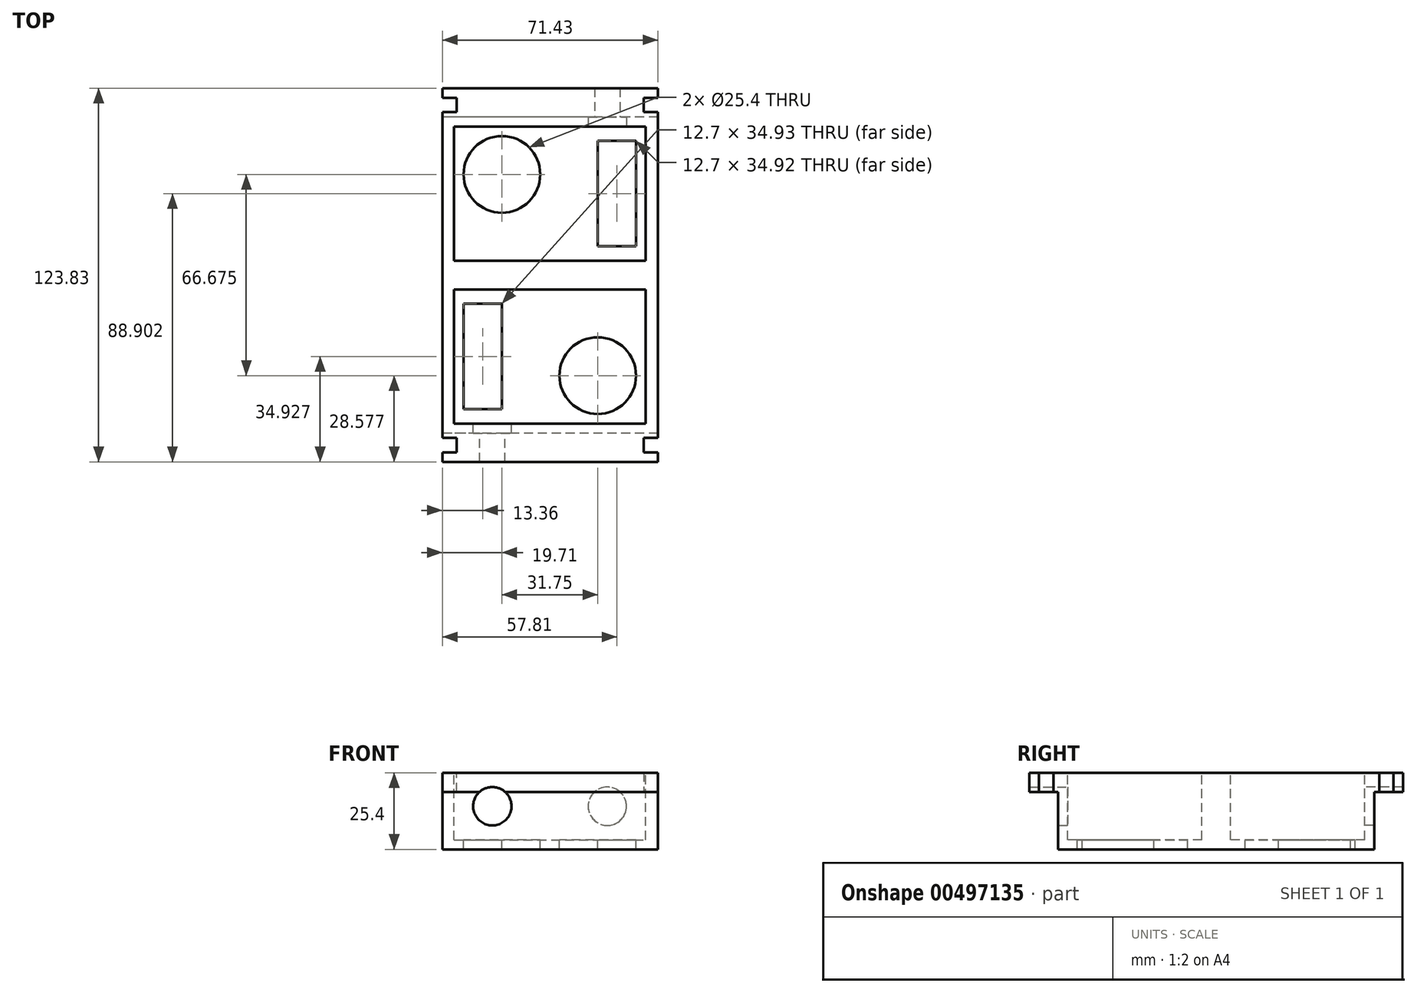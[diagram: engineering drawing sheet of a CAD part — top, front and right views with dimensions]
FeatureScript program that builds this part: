
annotation { "Feature Type Name" : "Feature", "Feature Type Description" : "" }
export const myFeature = defineFeature(function(context is Context, id is Id, definition is map)
    precondition{}
    {
        {
            var Q0;
            Q0=qCreatedBy(makeId("Top.planeOp"),FACE);
            var sketch = newSketch(context, id + "F0", { "sketchPlane" : qUnion([Q0])});
            skLineSegment(sketch, "E0.bottom", {"start": v(-33.34, 67.9) * mm, "end": v(38.09, 67.9) * mm});
            skLineSegment(sketch, "E0.top", {"start": v(-33.34, -55.92) * mm, "end": v(38.09, -55.92) * mm});
            skLineSegment(sketch, "E0.left", {"start": v(-33.34, 67.9) * mm, "end": v(-33.34, -55.92) * mm});
            skLineSegment(sketch, "E0.right", {"start": v(38.09, 67.9) * mm, "end": v(38.09, -55.92) * mm});
            skSolve(sketch);
        }
        {
            var Q0;
            Q0=makeQuery(id+"F0.imprint","IMPRINT",FACE,{"disambiguationData":[TD([[makeQuery(id+"F0.imprint","IMPRINT",EDGE,{"derivedFrom":sQuery(id+"F0.wireOp",EDGE,"E0.bottom")}),-1.0]])]});
            extrude(context, id + "F1", {"entities" : qUnion([Q0]), "depth" : 25.4 * mm});
        }
        {
            var Q0;
            Q0=makeQuery(id+"F1.opExtrude","CAP_FACE",FACE,{"disambiguationData":[OSD([sQuery(id+"F0.wireOp",EDGE,"E0.bottom"),sQuery(id+"F0.wireOp",EDGE,"E0.top"),sQuery(id+"F0.wireOp",EDGE,"E0.left"),sQuery(id+"F0.wireOp",EDGE,"E0.right")])],"isStart":false});
            var sketch = newSketch(context, id + "F2", { "sketchPlane" : qUnion([Q0])});
            skLineSegment(sketch, "E1.bottom", {"start": v(-29.5, 55.2) * mm, "end": v(34, 55.2) * mm});
            skLineSegment(sketch, "E1.top", {"start": v(-29.5, 10.76) * mm, "end": v(34, 10.76) * mm});
            skLineSegment(sketch, "E1.left", {"start": v(-29.5, 55.2) * mm, "end": v(-29.5, 10.76) * mm});
            skLineSegment(sketch, "E1.right", {"start": v(34, 55.2) * mm, "end": v(34, 10.76) * mm});
            skLineSegment(sketch, "E2.bottom", {"start": v(-29.5, 1.23) * mm, "end": v(34, 1.23) * mm});
            skLineSegment(sketch, "E2.top", {"start": v(-29.5, -43.22) * mm, "end": v(34, -43.22) * mm});
            skLineSegment(sketch, "E2.left", {"start": v(-29.5, 1.23) * mm, "end": v(-29.5, -43.22) * mm});
            skLineSegment(sketch, "E2.right", {"start": v(34, 1.23) * mm, "end": v(34, -43.22) * mm});
            skSolve(sketch);
        }
        {
            var Q0;
            Q0=makeQuery(id+"F2.imprint","IMPRINT",FACE,{"disambiguationData":[TD([[makeQuery(id+"F2.imprint","IMPRINT",EDGE,{"derivedFrom":sQuery(id+"F2.wireOp",EDGE,"E1.bottom")}),-1.0]])]});
            var Q1;
            Q1=makeQuery(id+"F2.imprint","IMPRINT",FACE,{"disambiguationData":[TD([[makeQuery(id+"F2.imprint","IMPRINT",EDGE,{"derivedFrom":sQuery(id+"F2.wireOp",EDGE,"E2.bottom")}),-1.0]])]});
            extrude(context, id + "F3", {"entities" : qUnion([Q0, Q1]), "operationType" : NewBodyOperationType.REMOVE, "oppositeDirection" : true, "depth" : 22.22 * mm});
        }
        {
            var Q0;
            Q0=makeQuery(id+"F1.opExtrude","SWEPT_FACE",FACE,{"disambiguationData":[OSD([sQuery(id+"F0.wireOp",EDGE,"E0.right")])]});
            var sketch = newSketch(context, id + "F4", { "sketchPlane" : qUnion([Q0])});
            skLineSegment(sketch, "E3.bottom", {"start": v(64.73, 25.4) * mm, "end": v(59.97, 25.4) * mm});
            skLineSegment(sketch, "E3.top", {"start": v(64.73, 0) * mm, "end": v(59.97, 0) * mm});
            skLineSegment(sketch, "E3.left", {"start": v(64.73, 25.4) * mm, "end": v(64.73, 0) * mm});
            skLineSegment(sketch, "E3.right", {"start": v(59.97, 25.4) * mm, "end": v(59.97, 0) * mm});
            skLineSegment(sketch, "E4.bottom", {"start": v(-47.98, 25.4) * mm, "end": v(-52.74, 25.4) * mm});
            skLineSegment(sketch, "E4.top", {"start": v(-47.98, 0) * mm, "end": v(-52.74, 0) * mm});
            skLineSegment(sketch, "E4.left", {"start": v(-47.98, 25.4) * mm, "end": v(-47.98, 0) * mm});
            skLineSegment(sketch, "E4.right", {"start": v(-52.74, 25.4) * mm, "end": v(-52.74, 0) * mm});
            skSolve(sketch);
        }
        {
            var Q0;
            Q0=makeQuery(id+"F4.imprint","IMPRINT",FACE,{"disambiguationData":[TD([[makeQuery(id+"F4.imprint","IMPRINT",EDGE,{"derivedFrom":sQuery(id+"F4.wireOp",EDGE,"E3.bottom")}),1.0]])]});
            var Q1;
            Q1=makeQuery(id+"F4.imprint","IMPRINT",FACE,{"disambiguationData":[TD([[makeQuery(id+"F4.imprint","IMPRINT",EDGE,{"derivedFrom":sQuery(id+"F4.wireOp",EDGE,"E4.bottom")}),1.0]])]});
            extrude(context, id + "F5", {"entities" : qUnion([Q0, Q1]), "operationType" : NewBodyOperationType.REMOVE, "oppositeDirection" : true, "depth" : 4.76 * mm});
        }
        {
            var Q0;
            Q0=makeQuery(id+"F1.opExtrude","SWEPT_FACE",FACE,{"disambiguationData":[OSD([sQuery(id+"F0.wireOp",EDGE,"E0.left")])]});
            var sketch = newSketch(context, id + "F6", { "sketchPlane" : qUnion([Q0])});
            skLineSegment(sketch, "E5.bottom", {"start": v(-64.73, 0) * mm, "end": v(-59.97, 0) * mm});
            skLineSegment(sketch, "E5.top", {"start": v(-64.73, 25.4) * mm, "end": v(-59.97, 25.4) * mm});
            skLineSegment(sketch, "E5.left", {"start": v(-64.73, 0) * mm, "end": v(-64.73, 25.4) * mm});
            skLineSegment(sketch, "E5.right", {"start": v(-59.97, 0) * mm, "end": v(-59.97, 25.4) * mm});
            skLineSegment(sketch, "E6.bottom", {"start": v(47.98, 0) * mm, "end": v(52.74, 0) * mm});
            skLineSegment(sketch, "E6.top", {"start": v(47.98, 25.4) * mm, "end": v(52.74, 25.4) * mm});
            skLineSegment(sketch, "E6.left", {"start": v(47.98, 0) * mm, "end": v(47.98, 25.4) * mm});
            skLineSegment(sketch, "E6.right", {"start": v(52.74, 0) * mm, "end": v(52.74, 25.4) * mm});
            skSolve(sketch);
        }
        {
            var Q0;
            Q0=makeQuery(id+"F6.imprint","IMPRINT",FACE,{"disambiguationData":[TD([[makeQuery(id+"F6.imprint","IMPRINT",EDGE,{"derivedFrom":sQuery(id+"F6.wireOp",EDGE,"E5.bottom")}),1.0]])]});
            var Q1;
            Q1=makeQuery(id+"F6.imprint","IMPRINT",FACE,{"disambiguationData":[TD([[makeQuery(id+"F6.imprint","IMPRINT",EDGE,{"derivedFrom":sQuery(id+"F6.wireOp",EDGE,"E6.bottom")}),1.0]])]});
            extrude(context, id + "F7", {"entities" : qUnion([Q0, Q1]), "operationType" : NewBodyOperationType.REMOVE, "oppositeDirection" : true, "depth" : 4.76 * mm});
        }
        {
            var Q0;
            Q0=makeQuery(id+"F1.opExtrude","CAP_FACE",FACE,{"disambiguationData":[OSD([sQuery(id+"F0.wireOp",EDGE,"E0.bottom"),sQuery(id+"F0.wireOp",EDGE,"E0.top"),sQuery(id+"F0.wireOp",EDGE,"E0.left"),sQuery(id+"F0.wireOp",EDGE,"E0.right")])],"isStart":true});
            var sketch = newSketch(context, id + "F8", { "sketchPlane" : qUnion([Q0])});
            skLineSegment(sketch, "E7.bottom", {"start": v(38.09, -67.9) * mm, "end": v(-33.34, -67.9) * mm});
            skLineSegment(sketch, "E7.top", {"start": v(38.09, -58.38) * mm, "end": v(-33.34, -58.38) * mm});
            skLineSegment(sketch, "E7.left", {"start": v(38.09, -67.9) * mm, "end": v(38.09, -58.38) * mm});
            skLineSegment(sketch, "E7.right", {"start": v(-33.34, -67.9) * mm, "end": v(-33.34, -58.38) * mm});
            skSolve(sketch);
        }
        {
            var Q0;
            {var subQ13=sQuery(id+"F8.wireOp",EDGE,"E7.bottom");Q0=makeQuery(id+"F8.imprint","IMPRINT",FACE,{"disambiguationData":[TD([[makeQuery(id+"F8.imprint","IMPRINT",EDGE,{"derivedFrom":subQ13}),1.0]])]});}
            extrude(context, id + "F9", {"entities" : qUnion([Q0]), "operationType" : NewBodyOperationType.REMOVE, "oppositeDirection" : true, "depth" : 19.05 * mm});
        }
        {
            var Q0;
            Q0=makeQuery(id+"F1.opExtrude","CAP_FACE",FACE,{"disambiguationData":[OSD([sQuery(id+"F0.wireOp",EDGE,"E0.bottom"),sQuery(id+"F0.wireOp",EDGE,"E0.top"),sQuery(id+"F0.wireOp",EDGE,"E0.left"),sQuery(id+"F0.wireOp",EDGE,"E0.right")])],"isStart":true});
            var sketch = newSketch(context, id + "F10", { "sketchPlane" : qUnion([Q0])});
            skLineSegment(sketch, "E8.bottom", {"start": v(38.09, 55.92) * mm, "end": v(-33.34, 55.92) * mm});
            skLineSegment(sketch, "E8.top", {"start": v(38.09, 46.4) * mm, "end": v(-33.34, 46.4) * mm});
            skLineSegment(sketch, "E8.left", {"start": v(38.09, 55.92) * mm, "end": v(38.09, 46.4) * mm});
            skLineSegment(sketch, "E8.right", {"start": v(-33.34, 55.92) * mm, "end": v(-33.34, 46.4) * mm});
            skSolve(sketch);
        }
        {
            var Q0;
            {var subQ6=sQuery(id+"F10.wireOp",EDGE,"E8.bottom");Q0=makeQuery(id+"F10.imprint","IMPRINT",FACE,{"disambiguationData":[TD([[makeQuery(id+"F10.imprint","IMPRINT",EDGE,{"derivedFrom":subQ6}),-1.0]])]});}
            extrude(context, id + "F11", {"entities" : qUnion([Q0]), "operationType" : NewBodyOperationType.REMOVE, "oppositeDirection" : true, "depth" : 19.05 * mm});
        }
        {
            var Q0;
            Q0=makeQuery(id+"F3.boolean.opBoolean","COPY",FACE,{"derivedFrom":makeQuery(id+"F3.opExtrude","CAP_FACE",FACE,{"disambiguationData":[OSD([sQuery(id+"F2.wireOp",EDGE,"E1.bottom"),sQuery(id+"F2.wireOp",EDGE,"E1.top"),sQuery(id+"F2.wireOp",EDGE,"E1.left"),sQuery(id+"F2.wireOp",EDGE,"E1.right")])],"isStart":false})});
            var sketch = newSketch(context, id + "F12", { "sketchPlane" : qUnion([Q0])});
            skCircle(sketch, "E9", {"center": v(-13.63, 39.33) * mm, "radius": 12.7 * mm});
            skLineSegment(sketch, "E10.bottom", {"start": v(18.12, 15.52) * mm, "end": v(30.82, 15.52) * mm});
            skLineSegment(sketch, "E10.top", {"start": v(18.12, 50.44) * mm, "end": v(30.82, 50.44) * mm});
            skLineSegment(sketch, "E10.left", {"start": v(18.12, 15.52) * mm, "end": v(18.12, 50.44) * mm});
            skLineSegment(sketch, "E10.right", {"start": v(30.82, 15.52) * mm, "end": v(30.82, 50.44) * mm});
            skCircle(sketch, "E11", {"center": v(18.12, -27.34) * mm, "radius": 12.7 * mm});
            skLineSegment(sketch, "E12.bottom", {"start": v(-26.33, -38.46) * mm, "end": v(-13.63, -38.46) * mm});
            skLineSegment(sketch, "E12.top", {"start": v(-26.33, -3.53) * mm, "end": v(-13.63, -3.53) * mm});
            skLineSegment(sketch, "E12.left", {"start": v(-26.33, -38.46) * mm, "end": v(-26.33, -3.53) * mm});
            skLineSegment(sketch, "E12.right", {"start": v(-13.63, -38.46) * mm, "end": v(-13.63, -3.53) * mm});
            skSolve(sketch);
        }
        {
            var Q0;
            Q0=makeQuery(id+"F12.imprint","IMPRINT",FACE,{"disambiguationData":[TD([[makeQuery(id+"F12.imprint","IMPRINT",EDGE,{"derivedFrom":sQuery(id+"F12.wireOp",EDGE,"E9")}),1.0]])]});
            var Q1;
            Q1=makeQuery(id+"F12.imprint","IMPRINT",FACE,{"disambiguationData":[TD([[makeQuery(id+"F12.imprint","IMPRINT",EDGE,{"derivedFrom":sQuery(id+"F12.wireOp",EDGE,"E10.bottom")}),1.0]])]});
            var Q2;
            Q2=makeQuery(id+"F12.imprint","IMPRINT",FACE,{"disambiguationData":[TD([[makeQuery(id+"F12.imprint","IMPRINT",EDGE,{"derivedFrom":sQuery(id+"F12.wireOp",EDGE,"E12.bottom")}),1.0]])]});
            var Q3;
            Q3=makeQuery(id+"F12.imprint","IMPRINT",FACE,{"disambiguationData":[TD([[makeQuery(id+"F12.imprint","IMPRINT",EDGE,{"derivedFrom":sQuery(id+"F12.wireOp",EDGE,"E11")}),1.0]])]});
            extrude(context, id + "F13", {"entities" : qUnion([Q0, Q1, Q2, Q3]), "operationType" : NewBodyOperationType.REMOVE, "oppositeDirection" : true, "depth" : 6.35 * mm});
        }
        {
            var Q0;
            Q0=makeQuery(id+"F3.boolean.opBoolean","COPY",FACE,{"derivedFrom":makeQuery(id+"F3.opExtrude","SWEPT_FACE",FACE,{"disambiguationData":[OSD([sQuery(id+"F2.wireOp",EDGE,"E1.bottom")])]})});
            var sketch = newSketch(context, id + "F14", { "sketchPlane" : qUnion([Q0])});
            skCircle(sketch, "E13", {"center": v(21.3, 14.29) * mm, "radius": 6.35 * mm});
            skSolve(sketch);
        }
        {
            var Q0;
            Q0=makeQuery(id+"F14.imprint","IMPRINT",FACE,{"disambiguationData":[TD([[makeQuery(id+"F14.imprint","IMPRINT",EDGE,{"derivedFrom":sQuery(id+"F14.wireOp",EDGE,"E13")}),1.0]])]});
            extrude(context, id + "F15", {"entities" : qUnion([Q0]), "operationType" : NewBodyOperationType.REMOVE, "oppositeDirection" : true, "depth" : 25.4 * mm});
        }
        {
            var Q0;
            Q0=makeQuery(id+"F3.boolean.opBoolean","COPY",FACE,{"derivedFrom":makeQuery(id+"F3.opExtrude","SWEPT_FACE",FACE,{"disambiguationData":[OSD([sQuery(id+"F2.wireOp",EDGE,"E2.top")])]})});
            var sketch = newSketch(context, id + "F16", { "sketchPlane" : qUnion([Q0])});
            skCircle(sketch, "E14", {"center": v(16.8, 14.29) * mm, "radius": 6.35 * mm});
            skSolve(sketch);
        }
        {
            var Q0;
            Q0=makeQuery(id+"F16.imprint","IMPRINT",FACE,{"disambiguationData":[TD([[makeQuery(id+"F16.imprint","IMPRINT",EDGE,{"derivedFrom":sQuery(id+"F16.wireOp",EDGE,"E14")}),1.0]])]});
            extrude(context, id + "F17", {"entities" : qUnion([Q0]), "operationType" : NewBodyOperationType.REMOVE, "oppositeDirection" : true, "depth" : 25.4 * mm});
        }
    });
